# Revit family: Drinking_Fountain-Haws_Corporation_1210S-1210SF
name_source: partatom
category: Plumbing Fixtures
revit_build: Autodesk Revit 2018 (Build: 20170223_1515(x64)
units: mm (PartAtom-declared; Revit-internal decimal feet)

## family parameters
Cut with Voids When Loaded = No
Host = Face
OmniClass Number = 23.31.31.11
OmniClass Title = Drinking Fountain With Coolers
Part Type = Normal
Room Calculation Point = No
Round Connector Dimension = Use Diameter
Shared = No

## types (2) — shared parameters
Assembly Code = D2010810
Bottle Filler = Yes
Clearance = Forward Approach
Default Elevation = 0' - 0"
Edition number = 1
Keynote = 15410.A1
Manufacturer = Haws Corporation
Material Enclosure = Metal - Haws Corporation - Satin Stainless Steel
Material Plastic = Plastic - Haws Corporation - Black
Product Page URL = https://www.hawsco.com
Product data url = https://www.bimobject.com
Tap Elevation Offset = 2' - 9"
URL = www.hawsco.com

## per-type parameters (varying)
| type | Description | Filter | Material Bracket | Material Bubbler | a |
| 1210S | Single, stainless steel electric water cooler with bottle filler only | No | Metal - Haws Corporation - Galvanized Steel | Metal - Haws Corporation - Flexible rubber | 2' - 3 27/32" |
| 1210SF | Single, stainless steel, filtered electric water cooler with bottle filler only | Yes | Metal - Haws Corporation - Silver Powder Coated Finish | Metal - Haws Corporation - Silver Powder Coated Finish | 2' - 6" |

note: column(s) folded — value = type name in every type: Model

## geometry (parser evidence)
native form markers: Sweep x5
no freeform markers — native parametric forms only
